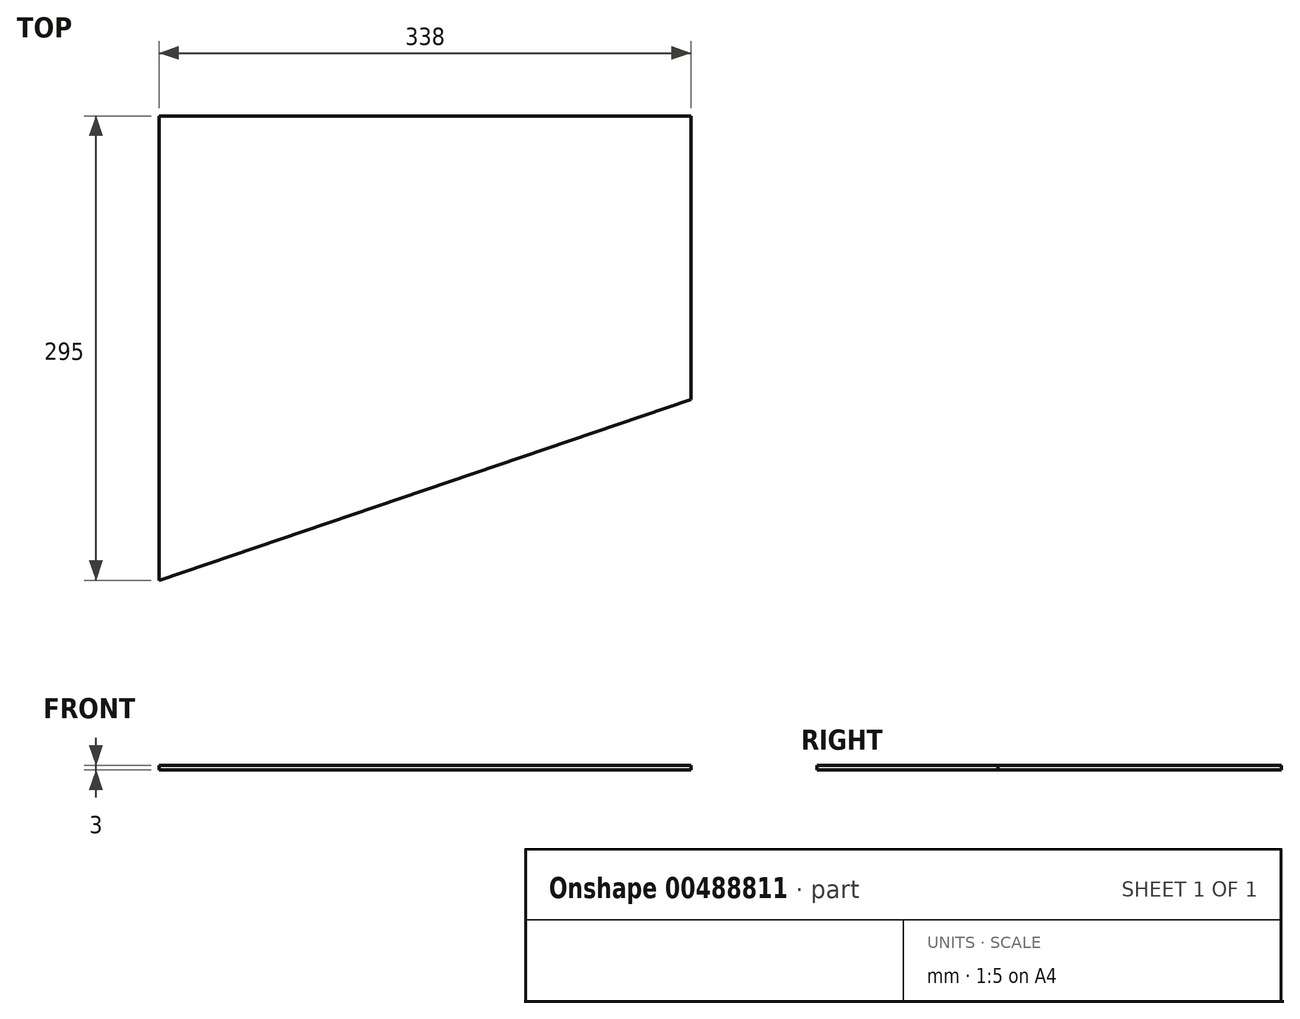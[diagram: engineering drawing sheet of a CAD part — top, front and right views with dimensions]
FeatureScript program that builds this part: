
annotation { "Feature Type Name" : "Feature", "Feature Type Description" : "" }
export const myFeature = defineFeature(function(context is Context, id is Id, definition is map)
    precondition{}
    {
        {
            var Q0;
            Q0=qCreatedBy(makeId("Top.planeOp"),FACE);
            var sketch = newSketch(context, id + "F0", { "sketchPlane" : qUnion([Q0])});
            skLineSegment(sketch, "E0", {"start": v(-185.79, 212.46) * mm, "end": v(-185.79, -82.54) * mm});
            skLineSegment(sketch, "E1", {"start": v(-185.79, 212.46) * mm, "end": v(152.21, 212.46) * mm});
            skLineSegment(sketch, "E2", {"start": v(152.21, 212.46) * mm, "end": v(152.21, 32.46) * mm});
            skLineSegment(sketch, "E3", {"start": v(152.21, 32.46) * mm, "end": v(-185.79, -82.54) * mm});
            skSolve(sketch);
        }
        {
            var Q0;
            Q0=makeQuery(id+"F0.imprint","IMPRINT",FACE,{"disambiguationData":[TD([[makeQuery(id+"F0.imprint","IMPRINT",EDGE,{"derivedFrom":sQuery(id+"F0.wireOp",EDGE,"E0")}),1.0]])]});
            extrude(context, id + "F1", {"entities" : qUnion([Q0]), "depth" : 3 * mm});
        }
    });
